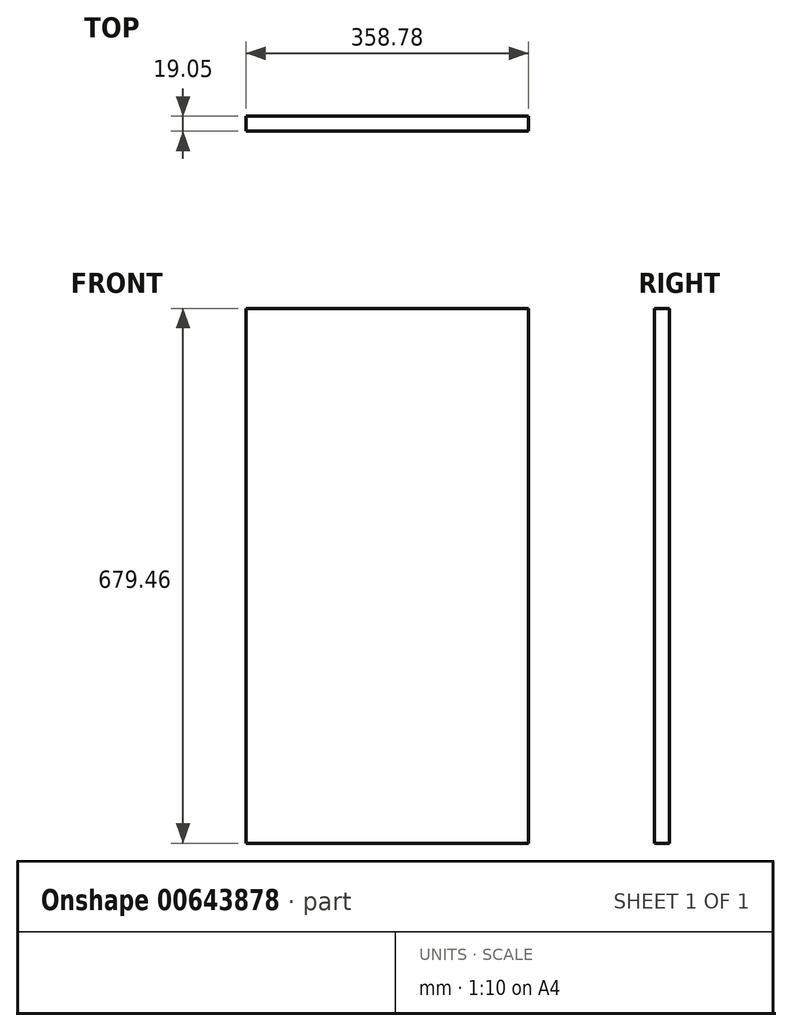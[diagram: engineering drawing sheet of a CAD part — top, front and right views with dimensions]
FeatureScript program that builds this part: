
annotation { "Feature Type Name" : "Feature", "Feature Type Description" : "" }
export const myFeature = defineFeature(function(context is Context, id is Id, definition is map)
    precondition{}
    {
        {
            var Q0;
            Q0=qCreatedBy(makeId("Front.planeOp"),FACE);
            var sketch = newSketch(context, id + "F0", { "sketchPlane" : qUnion([Q0])});
            skLineSegment(sketch, "E0.bottom", {"start": v(-179.39, 339.73) * mm, "end": v(179.39, 339.73) * mm});
            skLineSegment(sketch, "E0.top", {"start": v(-179.39, -339.73) * mm, "end": v(179.39, -339.73) * mm});
            skLineSegment(sketch, "E0.left", {"start": v(-179.39, 339.73) * mm, "end": v(-179.39, -339.73) * mm});
            skLineSegment(sketch, "E0.right", {"start": v(179.39, 339.73) * mm, "end": v(179.39, -339.73) * mm});
            skPoint(sketch, "E0.middle", {"position": v(0, 0) * mm});
            skSolve(sketch);
        }
        {
            var Q0;
            Q0=makeQuery(id+"F0.imprint","IMPRINT",FACE,{"disambiguationData":[TD([[makeQuery(id+"F0.imprint","IMPRINT",EDGE,{"derivedFrom":sQuery(id+"F0.wireOp",EDGE,"E0.bottom")}),-1.0]])]});
            extrude(context, id + "F1", {"entities" : qUnion([Q0]), "depth" : 19.05 * mm, "offsetDistance" : 25.4 * mm});
        }
    });
